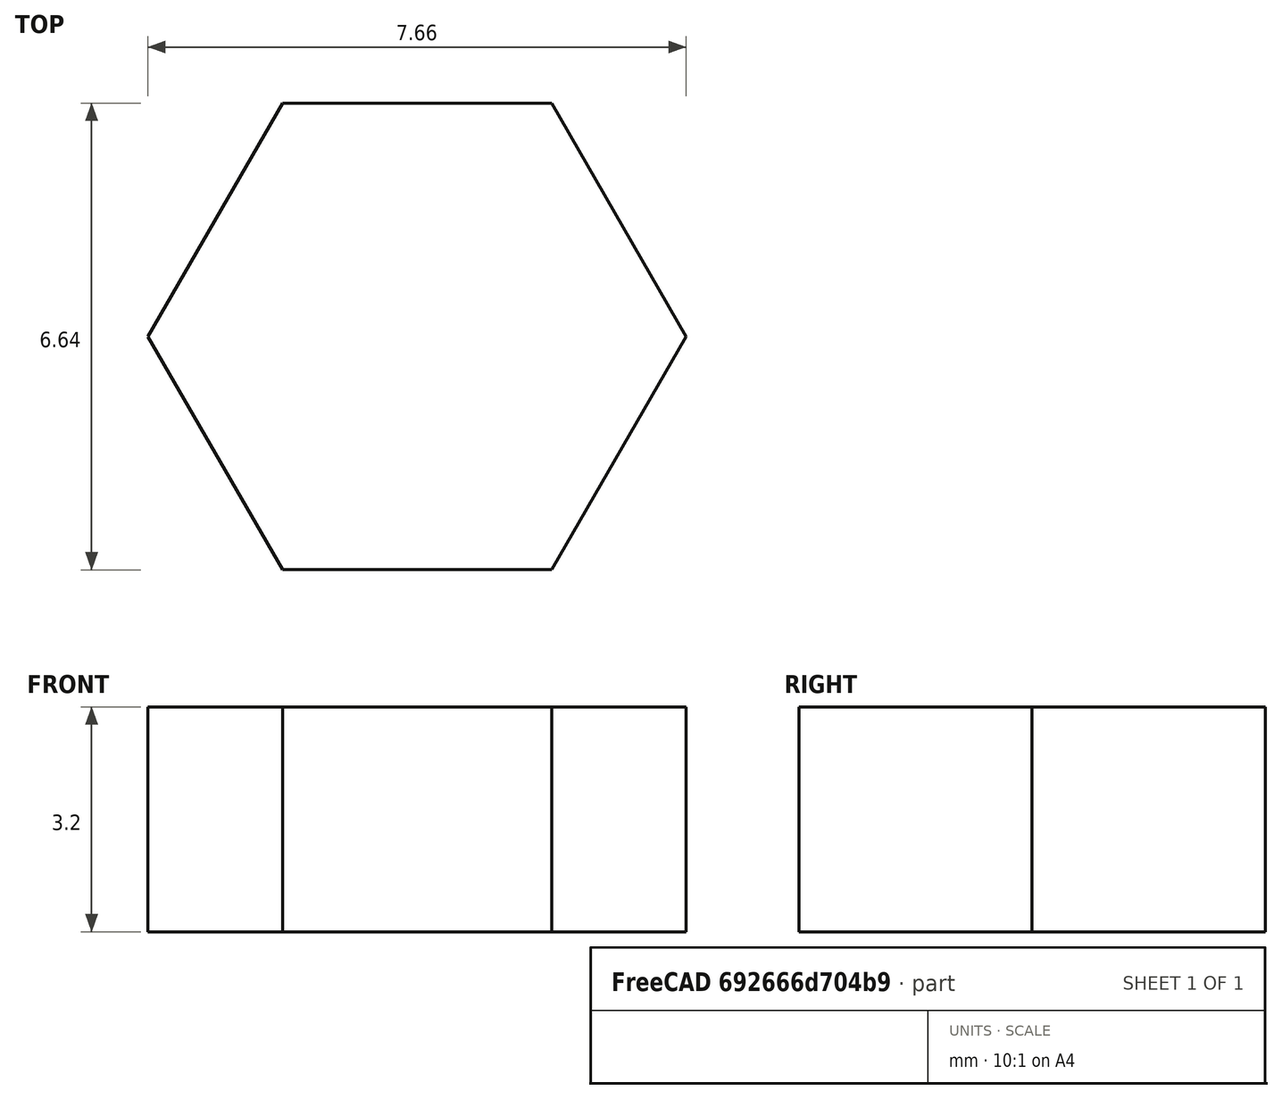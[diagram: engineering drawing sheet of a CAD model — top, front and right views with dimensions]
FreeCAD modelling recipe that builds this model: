
FCSTD DOCUMENT  (FreeCAD 0.21R0.20.1)
Label: Nut_DIN934_M3
License: All rights reserved
LicenseURL: https://en.wikipedia.org/wiki/All_rights_reserved
objects: Sketcher::SketchObject×1, Part::Extrusion×1
note: 2 computed .brp shape members not serialized (recipe doc carries the construction recipe); baked Part::Feature solids carry a one-line shape summary decoded from their .brp

FEATURE [Sketcher::SketchObject] Sketch
  FullyConstrained = true
  sketch-geometry (7):
    g0: LineSegment StartX=-3.83 StartY=0 StartZ=0 EndX=-1.915 EndY=-3.31688 EndZ=0
    g1: LineSegment StartX=-1.915 StartY=-3.31688 StartZ=0 EndX=1.915 EndY=-3.31688 EndZ=0
    g2: LineSegment StartX=1.915 StartY=-3.31688 StartZ=0 EndX=3.83 EndY=-9.0212e-12 EndZ=0
    g3: LineSegment StartX=3.83 StartY=-9.0212e-12 StartZ=0 EndX=1.915 EndY=3.31688 EndZ=0
    g4: LineSegment StartX=1.915 StartY=3.31688 StartZ=0 EndX=-1.915 EndY=3.31688 EndZ=0
    g5: LineSegment StartX=-1.915 StartY=3.31688 StartZ=0 EndX=-3.83 EndY=0 EndZ=0
    g6: Circle CenterX=0 CenterY=0 CenterZ=0 NormalX=0 NormalY=0 NormalZ=1 AngleXU=0 Radius=3.83
  constraints (16):
    c: Coincident(g0,g1)
    c: Coincident(g1,g2)
    c: Coincident(g2,g3)
    c: Coincident(g3,g4)
    c: Coincident(g4,g5)
    c: Coincident(g5,g0)
    c: Equal(g0, g1-g5) x5
    c: PointOnObject(g0,g6)
    c: PointOnObject(g1,g6)
    c: PointOnObject(g2,g6)
    c: PointOnObject(g3,g6)
    c: PointOnObject(g4,g6)
    c: PointOnObject(g5,g6)
    c: Coincident(g6,g-1)
    c: PointOnObject(g5,g-1)
    c: DistanceX(g0,g2) = 7.66
FEATURE [Part::Extrusion] Extrude  label="DIN934_M3"
  Base = -> Sketch
  Dir = (0,0,1)
  DirMode = 2
  FaceMakerClass = Part::FaceMakerBullseye
  LengthFwd = 3.2
  LengthRev = 0
  Solid = true
  Symmetric = false
